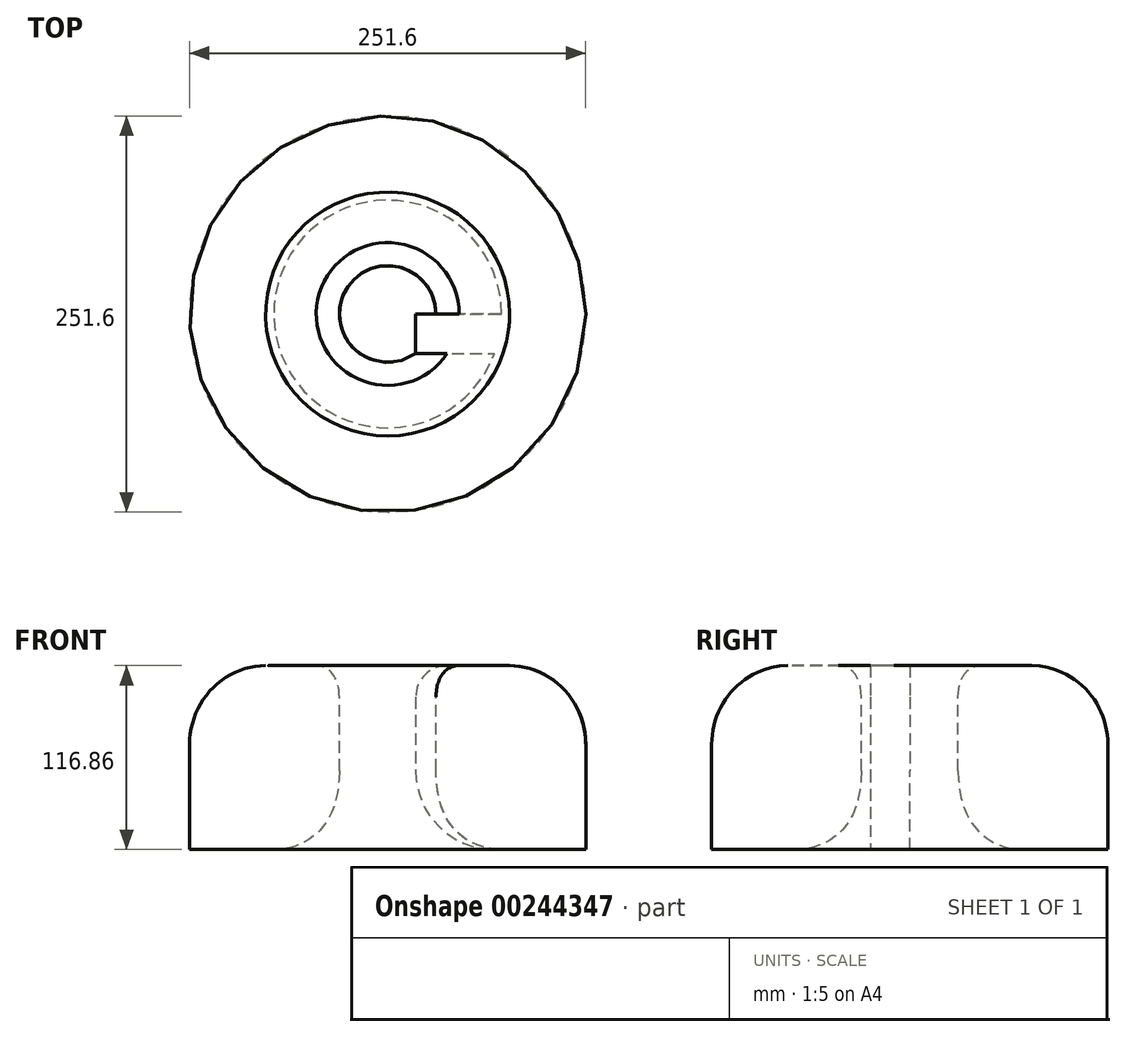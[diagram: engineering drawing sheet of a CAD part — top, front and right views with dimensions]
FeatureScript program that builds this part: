
annotation { "Feature Type Name" : "Feature", "Feature Type Description" : "" }
export const myFeature = defineFeature(function(context is Context, id is Id, definition is map)
    precondition{}
    {
        {
            var Q0;
            Q0=qCreatedBy(makeId("Front.planeOp"),FACE);
            var sketch = newSketch(context, id + "F0", { "sketchPlane" : qUnion([Q0])});
            skLineSegment(sketch, "E0.bottom", {"start": v(-23.9, 48.47) * mm, "end": v(11.54, 48.47) * mm});
            skLineSegment(sketch, "E0.top", {"start": v(6.1, -68.4) * mm, "end": v(61.54, -68.4) * mm});
            skLineSegment(sketch, "E0.left", {"start": v(-43.9, 28.47) * mm, "end": v(-43.9, -18.4) * mm});
            skLineSegment(sketch, "E0.right", {"start": v(61.54, -1.53) * mm, "end": v(61.54, -68.4) * mm});
            skPoint(sketch, "E1.visualSharp", {"position": v(-43.9, -68.4) * mm});
            skArc(sketch, "E1.filletArc", {"start": v(-43.9, -18.4) * mm, "mid": v(-29.26, -53.75) * mm, "end": v(6.1, -68.4) * mm});
            skPoint(sketch, "E2.visualSharp", {"position": v(61.54, 48.47) * mm});
            skArc(sketch, "E2.filletArc", {"start": v(61.54, -1.53) * mm, "mid": v(46.9, 33.83) * mm, "end": v(11.54, 48.47) * mm});
            skPoint(sketch, "E3.visualSharp", {"position": v(-43.9, 48.47) * mm});
            skArc(sketch, "E3.filletArc", {"start": v(-23.9, 48.47) * mm, "mid": v(-38.05, 42.61) * mm, "end": v(-43.9, 28.47) * mm});
            skLineSegment(sketch, "E4", {"start": v(-65.06, 71.71) * mm, "end": v(-65.06, -75.33) * mm});
            skSolve(sketch);
        }
        {
            var Q0;
            Q0=makeQuery(id+"F0.imprint","IMPRINT",FACE,{"disambiguationData":[TD([[makeQuery(id+"F0.imprint","IMPRINT",EDGE,{"derivedFrom":sQuery(id+"F0.wireOp",EDGE,"E0.bottom")}),-1.0]])]});
            extrude(context, id + "F1", {"entities" : qUnion([Q0]), "depth" : 25 * mm});
        }
        {
            var Q0;
            Q0=qCreatedBy(makeId("Front.planeOp"),FACE);
            var sketch = newSketch(context, id + "F2", { "sketchPlane" : qUnion([Q0])});
            skLineSegment(sketch, "E5", {"start": v(-61.75, 55.25) * mm, "end": v(-61.75, -55) * mm});
            skSolve(sketch);
        }
        {
            var Q0;
            Q0 = qSketchRegion(id + "F2", true);
            var Q1;
            Q1=makeQuery(id+"F1.opExtrude","CAP_FACE",FACE,{"disambiguationData":[OSD([sQuery(id+"F0.wireOp",EDGE,"E0.bottom"),sQuery(id+"F0.wireOp",EDGE,"E0.top"),sQuery(id+"F0.wireOp",EDGE,"E0.left"),sQuery(id+"F0.wireOp",EDGE,"E0.right"),sQuery(id+"F0.wireOp",EDGE,"E1.filletArc"),sQuery(id+"F0.wireOp",EDGE,"E2.filletArc"),sQuery(id+"F0.wireOp",EDGE,"E3.filletArc")])],"isStart":false});
            var Q2;
            Q2=sQuery(id+"F2.wireOp",EDGE,"E5");
            revolve(context, id + "F3", {"operationType" : NewBodyOperationType.ADD, "entities" : qUnion([Q0, Q1]), "axis" : qUnion([Q2]), "revolveType" : RevolveType.FULL});
        }
    });
